# Revit family: Hager-Vector-IP55-syst-DE-de
name_source: partatom
category: Electrical Equipment
units: mm (PartAtom-declared; Revit-internal decimal feet)

## family parameters
Cut with Voids When Loaded = No
Host = Face
Panel Configuration = Two Columns, Circuits Across
Part Type = Panelboard
Room Calculation Point = No
Round Connector Dimension = Use Diameter
Shared = No

## types (3) — shared parameters
EF000003 - Montageart = EV000384 - Aufputz
EF000007 - Farbe = EV000270 - grau
EF000116 - RAL-Nummer = 7035
EF000118 - Mit Montageplatte = No
EF000266 - Anzahl der Reihen = 1
EF000339 - Art der Abdeckung = EV004216 - Tür
EF001062 - EMV-Ausführung = No
EF001088 - Anbaumöglichkeit = Yes
EF001134 - DIN-Schiene = Yes
EF001596 - Werkstoff des Gehäuses = EV000139 - Kunststoff
EF004462 - Art der Schließung = EV000154 - sonstige
EF006244 - Transparenter Deckel/Tür = Yes
EF006306 - Mit Schloss = No
EF009212 - Ausführung Deckel = EV000116 - geschlossen
EF015776 - Erdungsklemmenblock = No
EF015777 - Neutralleiterklemmenblock = No
EF015941 - Signaldurchlassende Tür = Yes
HG000001 - Anzahl der Spalten = 1
HG000002 - Mit tür = Yes
HG000003 - Bereich = Vector
HG000005 - Dicke = 3 mm  [stored 0.00984252 ft]
HG000006 - Unterputz = No
HG000009 - Doppelflügeligen Tür = No
HG000010 - Asymmetrische Türen = No
HG000011 - Leere Reihen von unten = No
HG000017 - Distanz zwischen den Polen = 18 mm  [stored 0.0590551 ft]
Manufacturer = Hager
Type Comments = Vector
zero-valued in all types: Default Elevation, EF000218 - Einbautiefe, EF000332 - Einbauhöhe, EF000846 - Einbaubreite, HG000007 - Anzahl der leeren Spalten, HG000008 - Anzahl der leeren Reihen

## per-type parameters (varying)
| type | EF000008 - Breite | EF000040 - Höhe | EF000049 - Tiefe | EF001131 - Innentiefe | EF002950 - Breite in Teilungseinheiten | EF005474 - Schutzart (IP) | HG000004 - Herstellerreferenz | Model |
| Aufputz IP55 B164 H190 T113 6 Teilungseinheiten - VE106D | 164 mm | 190 mm | 113 mm | 113 mm | 6 | EV006420 - IP55 | VE106D | VE106D |
| Aufputz IP65 B110 H175 T93 3 Teilungseinheiten - VE103D | 110 mm | 175 mm | 93 mm | 93 mm | 3 | EV006421 - IP65 | VE103D | VE103D |
| Aufputz IP65 B236 H210 T114 10 Teilungseinheiten - VE110D | 236 mm  [stored 0.774278 ft] | 210 mm  [stored 0.688976 ft] | 114 mm  [stored 0.374016 ft] | 114 mm  [stored 0.374016 ft] | 10 | EV006421 - IP65 | VE110D | VE110D |

note: [stored X ft] marks values corroborated as IEEE doubles in the binary element streams (Revit-internal decimal feet)

## geometry (parser evidence)
native form markers: Sweep x17
no freeform markers — native parametric forms only
